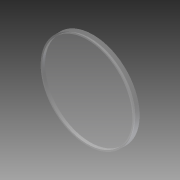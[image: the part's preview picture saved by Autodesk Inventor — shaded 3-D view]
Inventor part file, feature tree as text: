
AUTODESK INVENTOR PART (.ipt)
format: ipt  version: 2011 (Build 150239000, 239)  size: 80,384 bytes
history: native  units: in
note: dims shown in document units (in); Inventor stores cm internally (conversion verified against a paired STEP export)
features: extrude x2, sketch x2
ambient origin geometry x8: Origin, YZ Plane, XZ Plane, XY Plane, X Axis, Y Axis, Z Axis, Center Point
bodies: Solid1 (feature_tree)
feature tree (4):
  extrude  "Extrusion1"  TaperAngle=0.0deg  [1 undecoded]
  extrude  "Extrusion2"  Depth=1.55in
  sketch  "Sketch1"  dims[d0=0.0in d1=0.0in]
  sketch  "Sketch2"  dims[d2=1.6in d3=1.55in d4=0.05in d5=0.0in d6=0.05in d7=0.0in]
note: 1 required parameter value undecoded (feature->parameter linkage not recoverable at this tier; creation-order binding heuristic only, values carry confidence <= 0.55)
